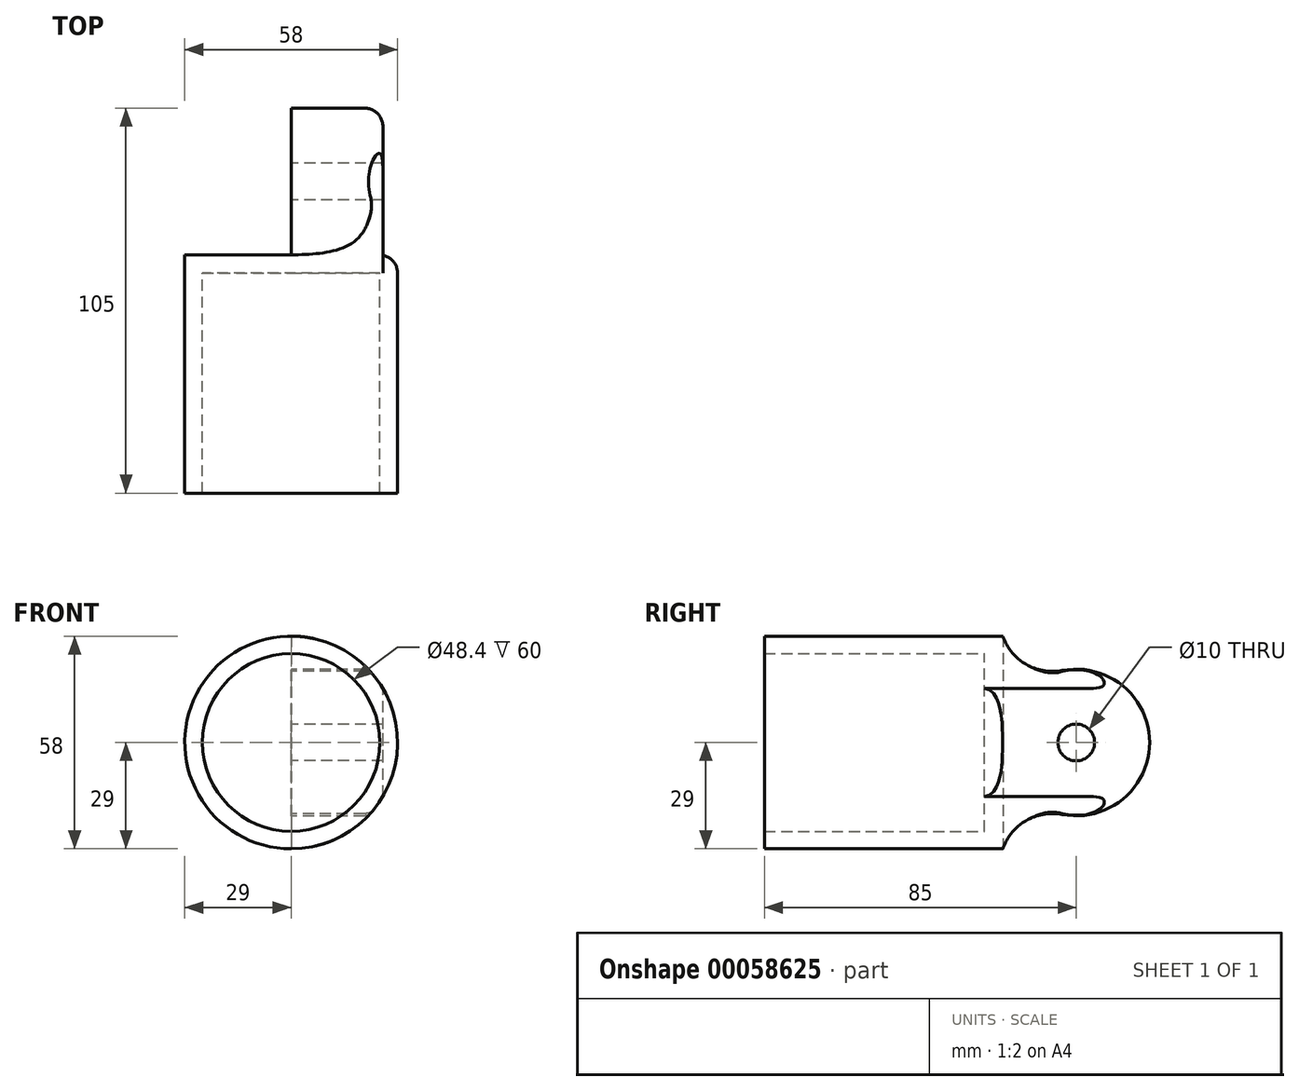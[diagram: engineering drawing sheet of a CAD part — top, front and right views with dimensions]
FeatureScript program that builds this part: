
annotation { "Feature Type Name" : "Feature", "Feature Type Description" : "" }
export const myFeature = defineFeature(function(context is Context, id is Id, definition is map)
    precondition{}
    {
        {
            var Q0;
            Q0=qCreatedBy(makeId("Front.planeOp"),FACE);
            var sketch = newSketch(context, id + "F0", { "sketchPlane" : qUnion([Q0])});
            skCircle(sketch, "E0", {"center": v(0, 0) * mm, "radius": 24.2 * mm});
            skCircle(sketch, "E1", {"center": v(0, 0) * mm, "radius": 29 * mm});
            skSolve(sketch);
        }
        {
            var Q0;
            Q0 = qSketchRegion(id + "F0", true);
            extrude(context, id + "F1", {"entities" : qUnion([Q0]), "depth" : 60 * mm});
        }
        {
            var Q0;
            Q0=makeQuery(id+"F1.opExtrude","CAP_FACE",FACE,{"disambiguationData":[OSD([sQuery(id+"F0.wireOp",EDGE,"E0"),sQuery(id+"F0.wireOp",EDGE,"E1")])],"isStart":true});
            var sketch = newSketch(context, id + "F2", { "sketchPlane" : qUnion([Q0])});
            skCircle(sketch, "E2", {"center": v(0, 0) * mm, "radius": 29 * mm});
            skSolve(sketch);
        }
        {
            var Q0;
            Q0 = qSketchRegion(id + "F2", true);
            extrude(context, id + "F3", {"entities" : qUnion([Q0]), "operationType" : NewBodyOperationType.ADD, "depth" : 5 * mm});
        }
        {
            var Q0;
            Q0=qCreatedBy(makeId("Right.planeOp"),FACE);
            var sketch = newSketch(context, id + "F4", { "sketchPlane" : qUnion([Q0])});
            skArc(sketch, "E3", {"start": v(21.21, -19.64) * mm, "mid": v(45, 0) * mm, "end": v(21.21, 19.64) * mm});
            skArc(sketch, "E4", {"start": v(5, 28.99) * mm, "mid": v(11.37, 21.3) * mm, "end": v(21.21, 19.64) * mm});
            skLineSegment(sketch, "E5", {"start": v(25, 0) * mm, "end": v(0, 0) * mm, "construction": true});
            skArc(sketch, "E6.MirrorCS", {"start": v(5, -28.99) * mm, "mid": v(11.37, -21.3) * mm, "end": v(21.21, -19.64) * mm});
            skLineSegment(sketch, "E7", {"start": v(5, 28.99) * mm, "end": v(5, -28.99) * mm});
            skCircle(sketch, "E8", {"center": v(25, 0) * mm, "radius": 5 * mm});
            skSolve(sketch);
        }
        {
            var Q0;
            Q0=makeQuery(id+"F4.imprint","IMPRINT",FACE,{"disambiguationData":[TD([[makeQuery(id+"F4.imprint","IMPRINT",EDGE,{"derivedFrom":sQuery(id+"F4.wireOp",EDGE,"E3")}),1.0]])]});
            extrude(context, id + "F5", {"entities" : qUnion([Q0]), "operationType" : NewBodyOperationType.ADD, "depth" : 25 * mm});
        }
        {
            var Q0;
            {var subQ1=sQuery(id+"F4.wireOp",EDGE,"E4");var subQ2=sQuery(id+"F4.wireOp",EDGE,"E7");Q0=makeQuery(id+"F5.boolean.opBoolean","SPLIT",FACE,{"disambiguationData":[TD([makeQuery(id+"F5.opExtrude","SWEPT_FACE",FACE,{"disambiguationData":[OSD([subQ1])]})])],"derivedFrom":makeQuery(id+"F5.opExtrude","SWEPT_FACE",FACE,{"disambiguationData":[OSD([subQ2])]})});}
            var Q1;
            {var subQ1=sQuery(id+"F4.wireOp",EDGE,"E6.MirrorCS");var subQ2=sQuery(id+"F4.wireOp",EDGE,"E7");Q1=makeQuery(id+"F5.boolean.opBoolean","SPLIT",FACE,{"disambiguationData":[TD([makeQuery(id+"F5.opExtrude","SWEPT_FACE",FACE,{"disambiguationData":[OSD([subQ1])]})])],"derivedFrom":makeQuery(id+"F5.opExtrude","SWEPT_FACE",FACE,{"disambiguationData":[OSD([subQ2])]})});}
            extrude(context, id + "F6", {"entities" : qUnion([Q0, Q1]), "operationType" : NewBodyOperationType.REMOVE, "endBound" : BoundingType.THROUGH_ALL, "oppositeDirection" : true, "depth" : 25 * mm});
        }
        {
            var Q0;
            Q0=makeQuery(id+"F5.opExtrude","CAP_EDGE",EDGE,{"disambiguationData":[OSD([sQuery(id+"F4.wireOp",EDGE,"E3")])],"isStart":false});
            var Q1;
            {var subQ0=sQuery(id+"F2.wireOp",EDGE,"E2");var subQ1=sQuery(id+"F4.wireOp",EDGE,"E7");Q1=makeQuery(id+"F5.boolean.opBoolean","SPLIT",EDGE,{"disambiguationData":[TD([makeQuery(id+"F1.opExtrude","SWEPT_FACE",FACE,{"disambiguationData":[OSD([sQuery(id+"F0.wireOp",EDGE,"E1")])]}),makeQuery(id+"F3.opExtrude","SWEPT_FACE",FACE,{"disambiguationData":[OSD([subQ0])]}),makeQuery(id+"F3.opExtrude","CAP_FACE",FACE,{"disambiguationData":[OSD([subQ0])],"isStart":false}),makeQuery(id+"F5.opExtrude","CAP_FACE",FACE,{"disambiguationData":[OSD([sQuery(id+"F4.wireOp",EDGE,"E3"),sQuery(id+"F4.wireOp",EDGE,"E4"),sQuery(id+"F4.wireOp",EDGE,"E6.MirrorCS"),subQ1,sQuery(id+"F4.wireOp",EDGE,"E8")])],"isStart":false}),makeQuery(id+"F5.opExtrude","SWEPT_FACE",FACE,{"disambiguationData":[OSD([subQ1])]})])],"derivedFrom":makeQuery(id+"F3.opExtrude","CAP_EDGE",EDGE,{"disambiguationData":[OSD([subQ0])],"isStart":false})});}
            var Q2;
            {var subQ0=sQuery(id+"F2.wireOp",EDGE,"E2");var subQ1=sQuery(id+"F4.wireOp",EDGE,"E4");var subQ2=makeQuery(id+"F5.opExtrude","SWEPT_FACE",FACE,{"disambiguationData":[OSD([subQ1])]});var subQ3=sQuery(id+"F4.wireOp",EDGE,"E7");Q2=makeQuery(id+"F6.boolean.opBoolean","INTERSECT",EDGE,{"derivedFrom":[subQ2,makeQuery(id+"F6.opExtrude","SWEPT_FACE",FACE,{"disambiguationData":[OSD([subQ0]),TDD([makeQuery(id+"F5.boolean.opBoolean","SPLIT",EDGE,{"disambiguationData":[TD([makeQuery(id+"F1.opExtrude","SWEPT_FACE",FACE,{"disambiguationData":[OSD([sQuery(id+"F0.wireOp",EDGE,"E1")])]}),makeQuery(id+"F3.opExtrude","SWEPT_FACE",FACE,{"disambiguationData":[OSD([subQ0])]}),makeQuery(id+"F3.opExtrude","CAP_FACE",FACE,{"disambiguationData":[OSD([subQ0])],"isStart":false}),makeQuery(id+"F5.opExtrude","CAP_FACE",FACE,{"disambiguationData":[OSD([sQuery(id+"F4.wireOp",EDGE,"E3"),subQ1,sQuery(id+"F4.wireOp",EDGE,"E6.MirrorCS"),subQ3,sQuery(id+"F4.wireOp",EDGE,"E8")])],"isStart":false}),subQ2,makeQuery(id+"F5.opExtrude","SWEPT_FACE",FACE,{"disambiguationData":[OSD([subQ3])]})])],"derivedFrom":makeQuery(id+"F3.opExtrude","CAP_EDGE",EDGE,{"disambiguationData":[OSD([subQ0])],"isStart":false})})])]})]});}
            var Q3;
            {var subQ0=sQuery(id+"F2.wireOp",EDGE,"E2");var subQ1=sQuery(id+"F4.wireOp",EDGE,"E6.MirrorCS");var subQ2=makeQuery(id+"F5.opExtrude","SWEPT_FACE",FACE,{"disambiguationData":[OSD([subQ1])]});var subQ3=sQuery(id+"F4.wireOp",EDGE,"E7");Q3=makeQuery(id+"F6.boolean.opBoolean","INTERSECT",EDGE,{"derivedFrom":[subQ2,makeQuery(id+"F6.opExtrude","SWEPT_FACE",FACE,{"disambiguationData":[OSD([subQ0]),TDD([makeQuery(id+"F5.boolean.opBoolean","SPLIT",EDGE,{"disambiguationData":[TD([makeQuery(id+"F1.opExtrude","SWEPT_FACE",FACE,{"disambiguationData":[OSD([sQuery(id+"F0.wireOp",EDGE,"E1")])]}),makeQuery(id+"F3.opExtrude","SWEPT_FACE",FACE,{"disambiguationData":[OSD([subQ0])]}),makeQuery(id+"F3.opExtrude","CAP_FACE",FACE,{"disambiguationData":[OSD([subQ0])],"isStart":false}),makeQuery(id+"F5.opExtrude","CAP_FACE",FACE,{"disambiguationData":[OSD([sQuery(id+"F4.wireOp",EDGE,"E3"),sQuery(id+"F4.wireOp",EDGE,"E4"),subQ1,subQ3,sQuery(id+"F4.wireOp",EDGE,"E8")])],"isStart":false}),subQ2,makeQuery(id+"F5.opExtrude","SWEPT_FACE",FACE,{"disambiguationData":[OSD([subQ3])]})])],"derivedFrom":makeQuery(id+"F3.opExtrude","CAP_EDGE",EDGE,{"disambiguationData":[OSD([subQ0])],"isStart":false})})])]})]});}
            fillet(context, id + "F7", {"entities" : qUnion([Q0, Q1, Q2, Q3]), "radius" : 5 * mm, "tangentPropagation" : true, "allowEdgeOverflow" : false});
        }
    });
